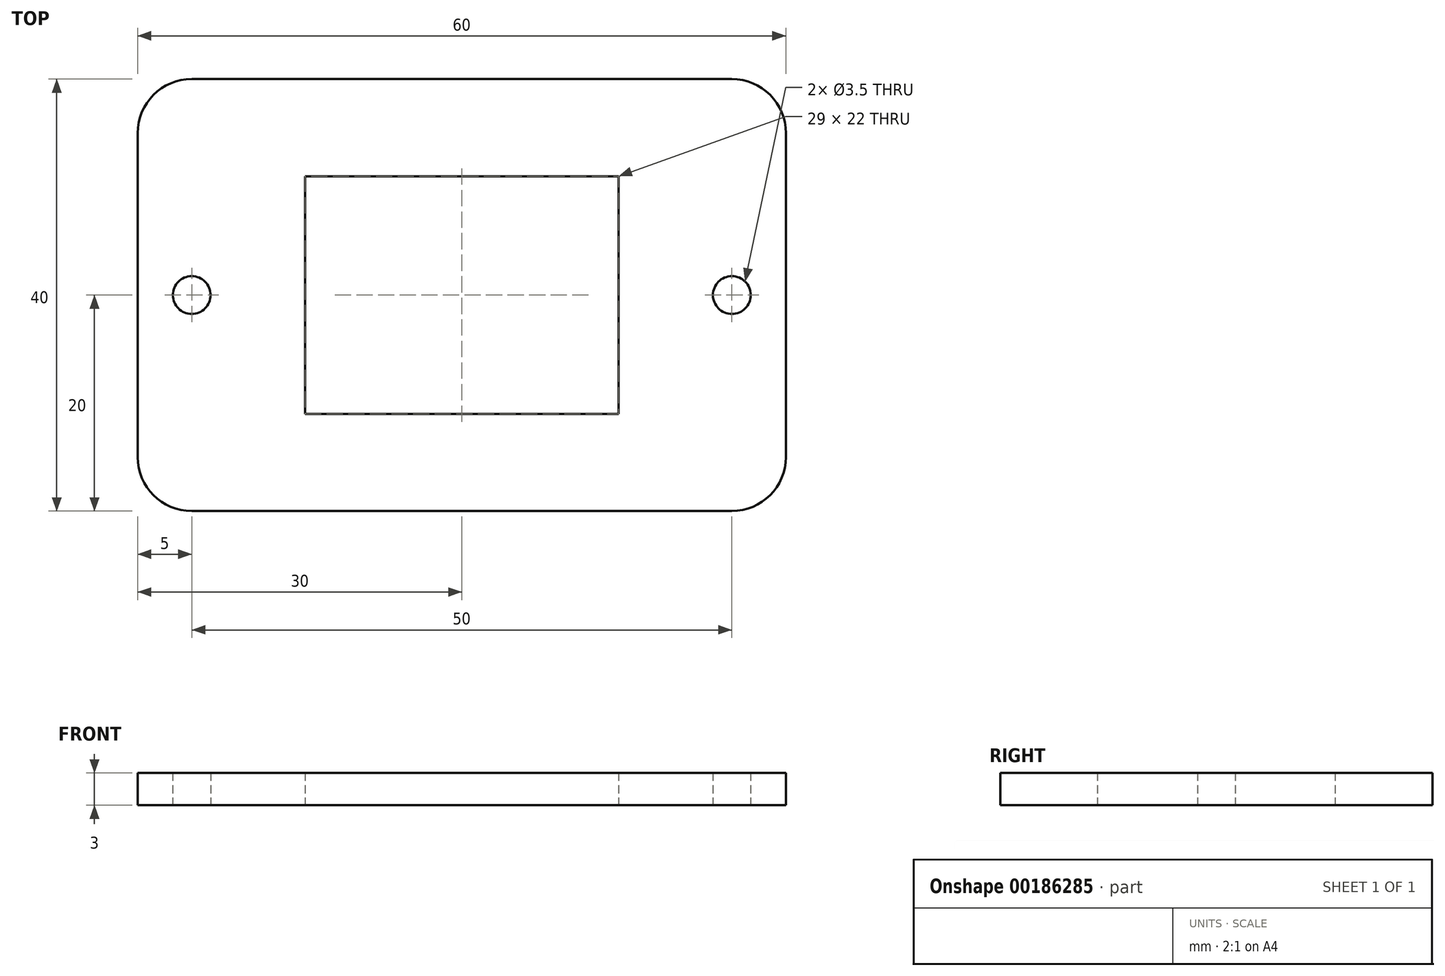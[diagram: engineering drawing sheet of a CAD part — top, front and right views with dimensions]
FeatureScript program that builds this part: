
annotation { "Feature Type Name" : "Feature", "Feature Type Description" : "" }
export const myFeature = defineFeature(function(context is Context, id is Id, definition is map)
    precondition{}
    {
        {
            var Q0;
            Q0=qCreatedBy(makeId("Top.planeOp"),FACE);
            var sketch = newSketch(context, id + "F0", { "sketchPlane" : qUnion([Q0])});
            skLineSegment(sketch, "E0.bottom", {"start": v(30, -20) * mm, "end": v(-30, -20) * mm});
            skLineSegment(sketch, "E0.top", {"start": v(30, 20) * mm, "end": v(-30, 20) * mm});
            skLineSegment(sketch, "E0.left", {"start": v(30, -20) * mm, "end": v(30, 20) * mm});
            skLineSegment(sketch, "E0.right", {"start": v(-30, -20) * mm, "end": v(-30, 20) * mm});
            skPoint(sketch, "E0.middle", {"position": v(0, 0) * mm});
            skLineSegment(sketch, "E1.bottom", {"start": v(14.5, -11) * mm, "end": v(-14.5, -11) * mm});
            skLineSegment(sketch, "E1.top", {"start": v(14.5, 11) * mm, "end": v(-14.5, 11) * mm});
            skLineSegment(sketch, "E1.left", {"start": v(14.5, -11) * mm, "end": v(14.5, 11) * mm});
            skLineSegment(sketch, "E1.right", {"start": v(-14.5, -11) * mm, "end": v(-14.5, 11) * mm});
            skPoint(sketch, "E2", {"position": v(25, 0) * mm});
            skPoint(sketch, "E3", {"position": v(-25, 0) * mm});
            skCircle(sketch, "E4", {"center": v(25, 0) * mm, "radius": 1.75 * mm});
            skCircle(sketch, "E5", {"center": v(-25, 0) * mm, "radius": 1.75 * mm});
            skSolve(sketch);
        }
        {
            var Q0;
            Q0=makeQuery(id+"F0.imprint","IMPRINT",FACE,{"disambiguationData":[TD([[makeQuery(id+"F0.imprint","IMPRINT",EDGE,{"derivedFrom":sQuery(id+"F0.wireOp",EDGE,"E0.bottom")}),-1.0]])]});
            extrude(context, id + "F1", {"entities" : qUnion([Q0]), "depth" : 3 * mm, "offsetDistance" : 25 * mm});
        }
        {
            var Q0;
            Q0=makeQuery(id+"F1.opExtrude","SWEPT_EDGE",EDGE,{"disambiguationData":[OSD([sQuery(id+"F0.wireOp",EDGE,"E0.bottom"),sQuery(id+"F0.wireOp",EDGE,"E0.right")])]});
            var Q1;
            Q1=makeQuery(id+"F1.opExtrude","SWEPT_EDGE",EDGE,{"disambiguationData":[OSD([sQuery(id+"F0.wireOp",EDGE,"E0.top"),sQuery(id+"F0.wireOp",EDGE,"E0.right")])]});
            var Q2;
            Q2=makeQuery(id+"F1.opExtrude","SWEPT_EDGE",EDGE,{"disambiguationData":[OSD([sQuery(id+"F0.wireOp",EDGE,"E0.top"),sQuery(id+"F0.wireOp",EDGE,"E0.left")])]});
            var Q3;
            Q3=makeQuery(id+"F1.opExtrude","SWEPT_EDGE",EDGE,{"disambiguationData":[OSD([sQuery(id+"F0.wireOp",EDGE,"E0.bottom"),sQuery(id+"F0.wireOp",EDGE,"E0.left")])]});
            fillet(context, id + "F2", {"entities" : qUnion([Q0, Q1, Q2, Q3]), "radius" : 5 * mm, "tangentPropagation" : true, "allowEdgeOverflow" : false});
        }
    });
